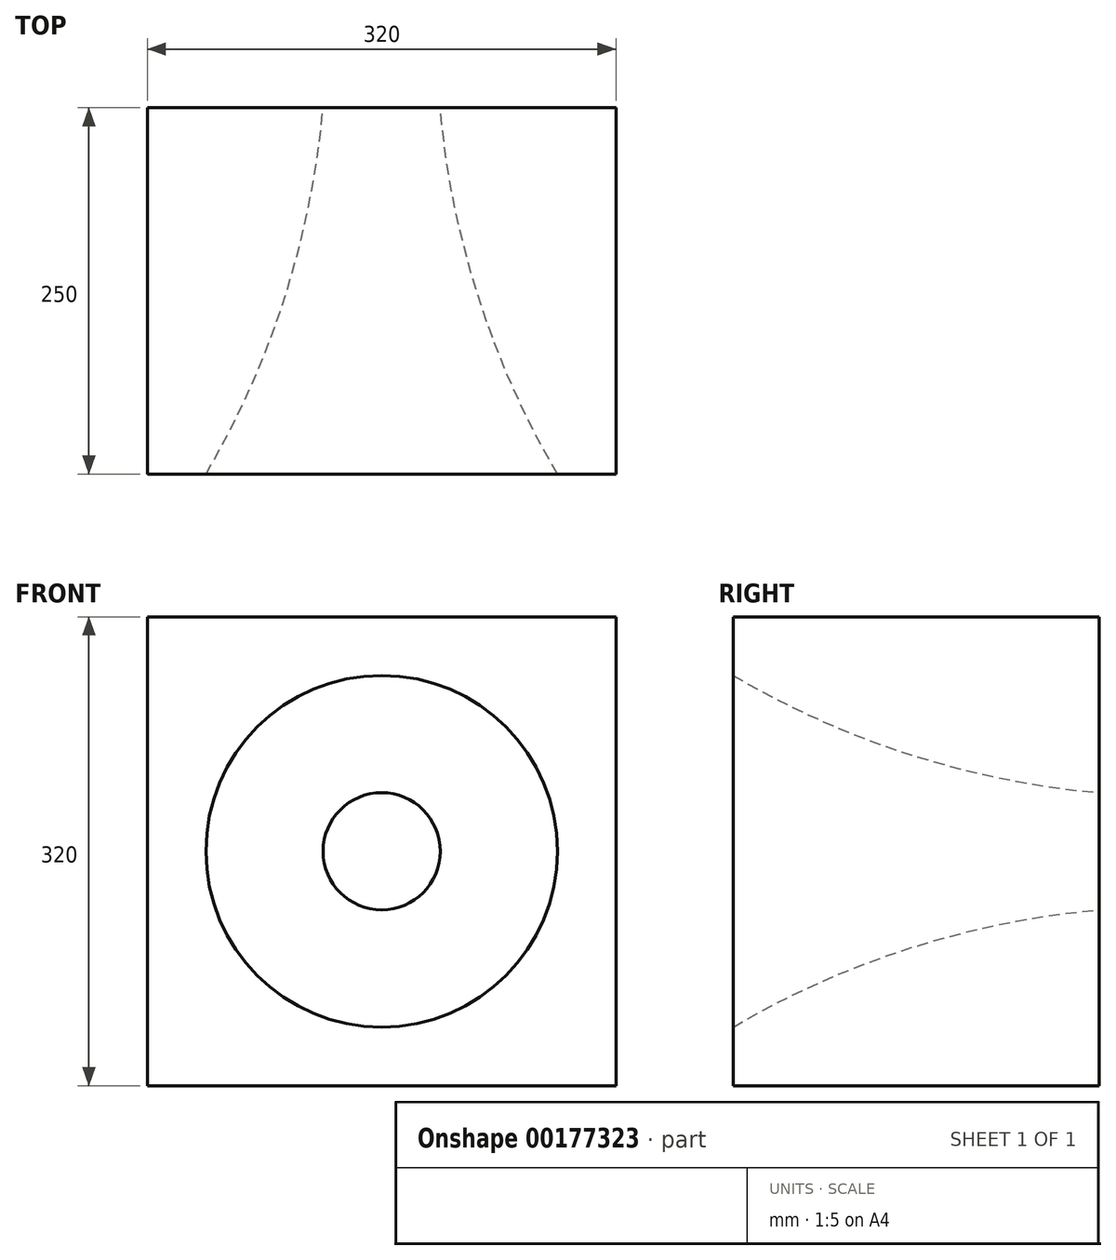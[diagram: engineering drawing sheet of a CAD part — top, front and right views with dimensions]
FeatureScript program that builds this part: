
annotation { "Feature Type Name" : "Feature", "Feature Type Description" : "" }
export const myFeature = defineFeature(function(context is Context, id is Id, definition is map)
    precondition{}
    {
        {
            var Q0;
            Q0=qCreatedBy(makeId("Front.planeOp"),FACE);
            cPlane(context, id + "F0", {"entities" : qUnion([Q0]), "cplaneType" : CPlaneType.OFFSET, "offset" : 250 * mm, "width" : 150 * mm, "height" : 150 * mm});
        }
        {
            var Q0;
            Q0=qCreatedBy(makeId("Front.planeOp"),FACE);
            var sketch = newSketch(context, id + "F1", { "sketchPlane" : qUnion([Q0])});
            skLineSegment(sketch, "E0.bottom", {"start": v(160, 160) * mm, "end": v(-160, 160) * mm});
            skLineSegment(sketch, "E0.top", {"start": v(160, -160) * mm, "end": v(-160, -160) * mm});
            skLineSegment(sketch, "E0.left", {"start": v(160, 160) * mm, "end": v(160, -160) * mm});
            skLineSegment(sketch, "E0.right", {"start": v(-160, 160) * mm, "end": v(-160, -160) * mm});
            skPoint(sketch, "E0.middle", {"position": v(0, 0) * mm});
            skSolve(sketch);
        }
        {
            var Q0;
            Q0=makeQuery(id+"F1.imprint","IMPRINT",FACE,{"disambiguationData":[TD([[makeQuery(id+"F1.imprint","IMPRINT",EDGE,{"derivedFrom":sQuery(id+"F1.wireOp",EDGE,"E0.bottom")}),1.0]])]});
            var Q1;
            Q1=qCreatedBy(id+"F0.planeOp",FACE);
            extrude(context, id + "F2", {"entities" : qUnion([Q0]), "endBound" : BoundingType.UP_TO_SURFACE, "endBoundEntityFace" : qUnion([Q1]), "depth" : 25 * mm});
        }
        {
            var Q0;
            Q0=qCreatedBy(makeId("Front.planeOp"),FACE);
            var sketch = newSketch(context, id + "F3", { "sketchPlane" : qUnion([Q0])});
            skCircle(sketch, "E1", {"center": v(0, 0) * mm, "radius": 40 * mm});
            skSolve(sketch);
        }
        {
            var Q0;
            Q0=qCreatedBy(id+"F0.planeOp",FACE);
            var sketch = newSketch(context, id + "F4", { "sketchPlane" : qUnion([Q0])});
            skCircle(sketch, "E2", {"center": v(0, 0) * mm, "radius": 120 * mm});
            skSolve(sketch);
        }
        {
            var Q0;
            Q0=qCreatedBy(makeId("Right.planeOp"),FACE);
            var sketch = newSketch(context, id + "F5", { "sketchPlane" : qUnion([Q0])});
            skArc(sketch, "E3", {"start": v(-250, 120) * mm, "mid": v(-129.43, 66.16) * mm, "end": v(0, 40) * mm});
            skSolve(sketch);
        }
        {
            var Q1;
            Q1 = qSketchRegion(id + "F3", true);
            var Q2;
            Q2 = qSketchRegion(id + "F4", true);
            var Q3;
            Q3=sQuery(id+"F5.wireOp",EDGE,"E3");
            loft(context, id + "F6", {"operationType" : NewBodyOperationType.REMOVE, "addGuides" : true, "sheetProfilesArray" : [{ "sheetProfileEntities" : qUnion([Q1]) }, { "sheetProfileEntities" : qUnion([Q2]) }], "guidesArray" : [{ "guideEntities" : qUnion([Q3]), "guideDerivativeType" : LoftGuideDerivativeType.DEFAULT, "guideDerivativeMagnitude" : 1 }]});
        }
    });
